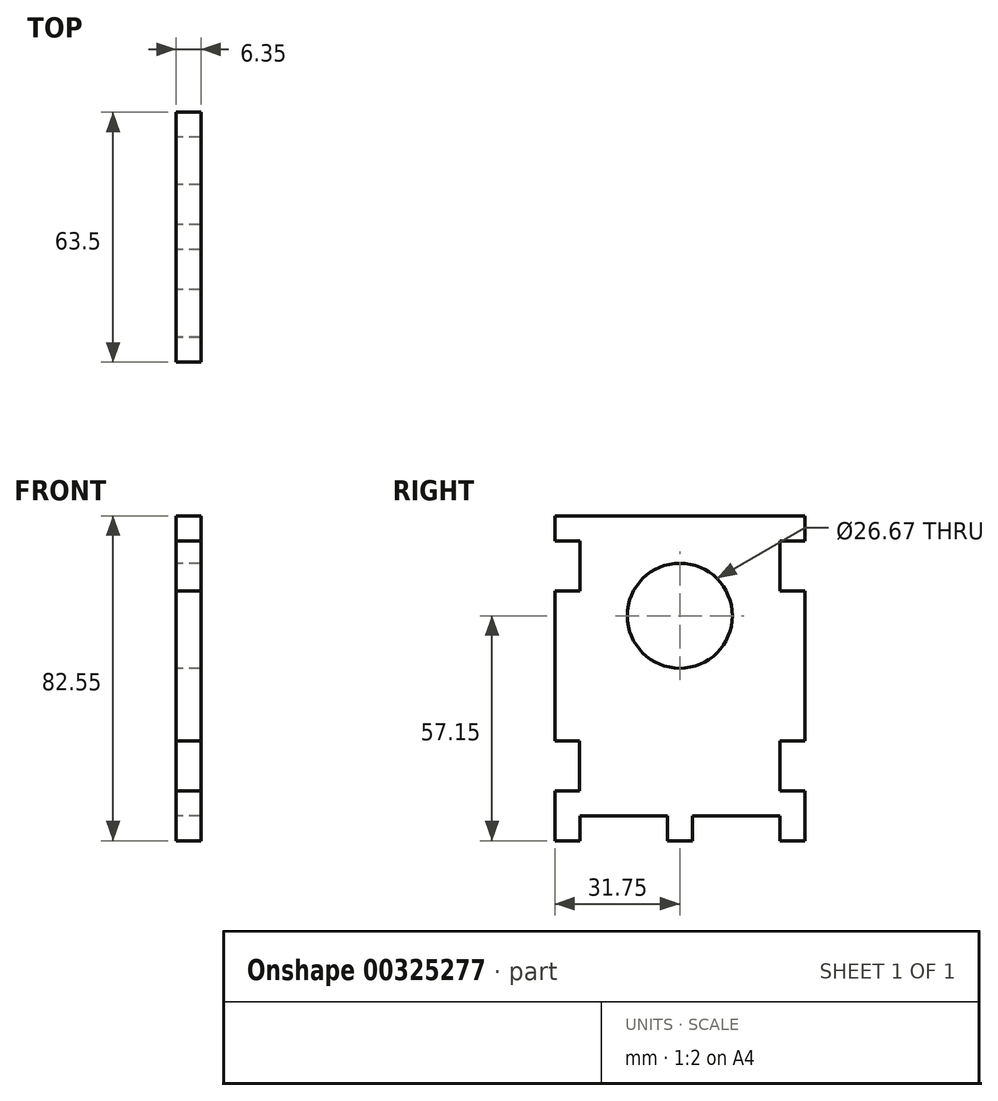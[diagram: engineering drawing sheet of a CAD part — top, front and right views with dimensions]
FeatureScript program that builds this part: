
annotation { "Feature Type Name" : "Feature", "Feature Type Description" : "" }
export const myFeature = defineFeature(function(context is Context, id is Id, definition is map)
    precondition{}
    {
        {
            var Q0;
            Q0=qCreatedBy(makeId("Right.planeOp"),FACE);
            var sketch = newSketch(context, id + "F0", { "sketchPlane" : qUnion([Q0])});
            skLineSegment(sketch, "E0", {"start": v(0, 0) * mm, "end": v(6.35, 0) * mm});
            skLineSegment(sketch, "E1", {"start": v(6.35, 0) * mm, "end": v(6.35, 6.35) * mm});
            skLineSegment(sketch, "E2", {"start": v(6.35, 6.35) * mm, "end": v(28.57, 6.35) * mm});
            skLineSegment(sketch, "E3", {"start": v(28.57, 6.35) * mm, "end": v(28.57, 0) * mm});
            skLineSegment(sketch, "E4", {"start": v(28.57, 0) * mm, "end": v(34.92, 0) * mm});
            skLineSegment(sketch, "E5", {"start": v(34.92, 0) * mm, "end": v(34.92, 6.35) * mm});
            skLineSegment(sketch, "E6", {"start": v(34.92, 6.35) * mm, "end": v(57.15, 6.35) * mm});
            skLineSegment(sketch, "E7", {"start": v(57.15, 6.35) * mm, "end": v(57.15, 0) * mm});
            skLineSegment(sketch, "E8", {"start": v(57.15, 0) * mm, "end": v(63.5, 0) * mm});
            skLineSegment(sketch, "E9", {"start": v(63.5, 0) * mm, "end": v(63.5, 12.7) * mm});
            skLineSegment(sketch, "E10", {"start": v(63.5, 12.7) * mm, "end": v(57.15, 12.7) * mm});
            skLineSegment(sketch, "E11", {"start": v(57.15, 12.7) * mm, "end": v(57.15, 25.4) * mm});
            skLineSegment(sketch, "E12", {"start": v(57.15, 25.4) * mm, "end": v(63.5, 25.4) * mm});
            skLineSegment(sketch, "E13", {"start": v(63.5, 25.4) * mm, "end": v(63.5, 63.5) * mm});
            skLineSegment(sketch, "E14", {"start": v(63.5, 63.5) * mm, "end": v(57.15, 63.5) * mm});
            skLineSegment(sketch, "E15", {"start": v(57.15, 63.5) * mm, "end": v(57.15, 76.2) * mm});
            skLineSegment(sketch, "E16", {"start": v(57.15, 76.2) * mm, "end": v(63.5, 76.2) * mm});
            skLineSegment(sketch, "E17", {"start": v(63.5, 76.2) * mm, "end": v(63.5, 82.55) * mm});
            skLineSegment(sketch, "E18", {"start": v(63.5, 82.55) * mm, "end": v(0, 82.55) * mm});
            skLineSegment(sketch, "E19", {"start": v(0, 82.55) * mm, "end": v(0, 76.2) * mm});
            skLineSegment(sketch, "E20", {"start": v(0, 76.2) * mm, "end": v(6.35, 76.2) * mm});
            skLineSegment(sketch, "E21", {"start": v(6.35, 76.2) * mm, "end": v(6.35, 63.5) * mm});
            skLineSegment(sketch, "E22", {"start": v(6.35, 63.5) * mm, "end": v(0, 63.5) * mm});
            skLineSegment(sketch, "E23", {"start": v(0, 63.5) * mm, "end": v(0, 25.4) * mm});
            skLineSegment(sketch, "E24", {"start": v(0, 25.4) * mm, "end": v(6.28, 25.4) * mm});
            skLineSegment(sketch, "E25", {"start": v(6.28, 25.4) * mm, "end": v(6.28, 12.7) * mm});
            skLineSegment(sketch, "E26", {"start": v(6.28, 12.7) * mm, "end": v(0, 12.7) * mm});
            skLineSegment(sketch, "E27", {"start": v(0, 12.7) * mm, "end": v(0, 0) * mm});
            skLineSegment(sketch, "E28", {"start": v(31.75, 82.55) * mm, "end": v(31.75, 0) * mm, "construction": true});
            skCircle(sketch, "E29", {"center": v(31.75, 57.15) * mm, "radius": 13.34 * mm});
            skSolve(sketch);
        }
        {
            var Q0;
            Q0=makeQuery(id+"F0.imprint","IMPRINT",FACE,{"disambiguationData":[TD([[makeQuery(id+"F0.imprint","IMPRINT",EDGE,{"derivedFrom":sQuery(id+"F0.wireOp",EDGE,"E0")}),1.0]])]});
            extrude(context, id + "F1", {"entities" : qUnion([Q0]), "depth" : 6.35 * mm});
        }
    });
